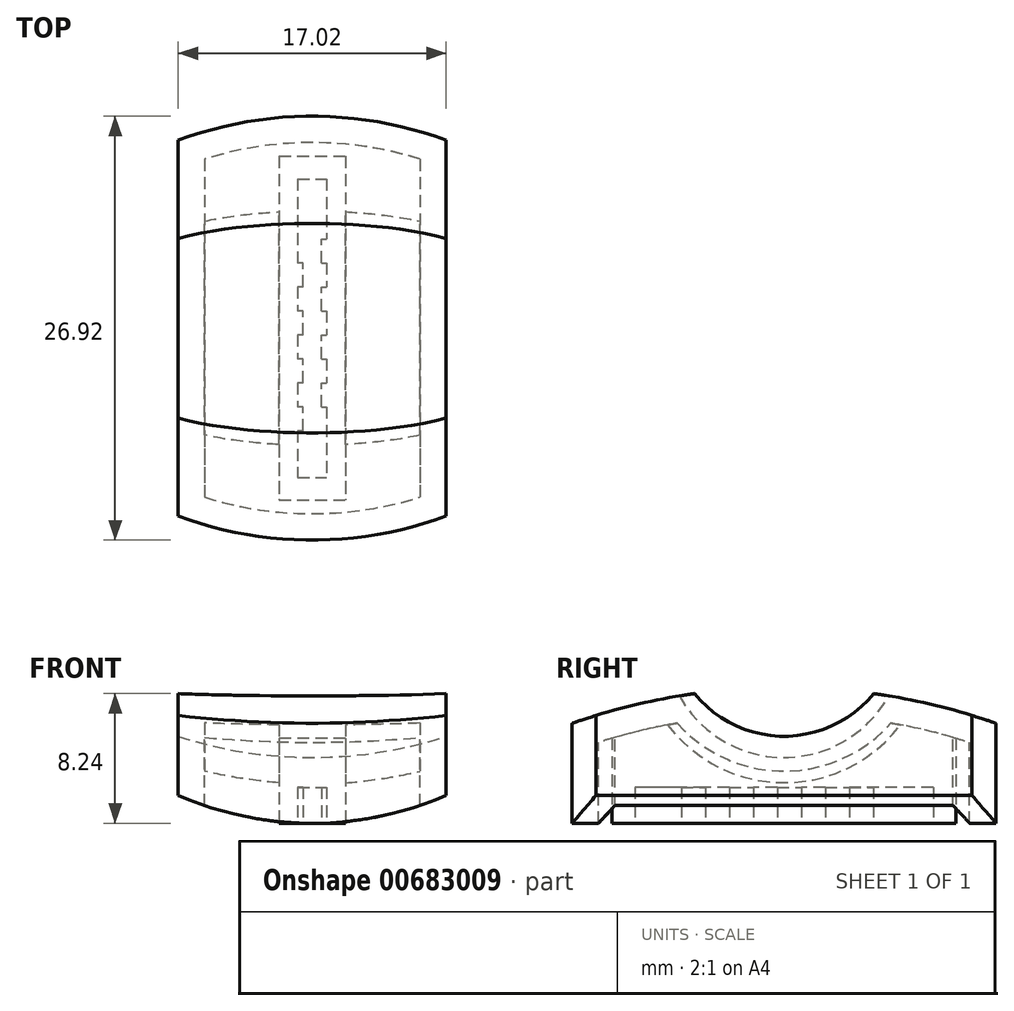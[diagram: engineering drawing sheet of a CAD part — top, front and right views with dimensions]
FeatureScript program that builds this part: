
annotation { "Feature Type Name" : "Feature", "Feature Type Description" : "" }
export const myFeature = defineFeature(function(context is Context, id is Id, definition is map)
    precondition{}
    {
        {
            var Q0;
            Q0=qCreatedBy(makeId("Top.planeOp"),FACE);
            var sketch = newSketch(context, id + "F0", { "sketchPlane" : qUnion([Q0])});
            skLineSegment(sketch, "E0.bottom", {"start": v(-8.5, 13.46) * mm, "end": v(8.5, 13.46) * mm});
            skLineSegment(sketch, "E0.top", {"start": v(-8.5, -13.46) * mm, "end": v(8.5, -13.46) * mm});
            skLineSegment(sketch, "E0.left", {"start": v(-8.5, 13.46) * mm, "end": v(-8.5, -13.46) * mm});
            skLineSegment(sketch, "E0.right", {"start": v(8.5, 13.46) * mm, "end": v(8.5, -13.46) * mm});
            skPoint(sketch, "E0.middle", {"position": v(0, 0) * mm});
            skSolve(sketch);
        }
        {
            var Q0;
            Q0 = qSketchRegion(id + "F0", true);
            extrude(context, id + "F1", {"entities" : qUnion([Q0]), "depth" : 8.64 * mm, "offsetDistance" : 25.4 * mm});
        }
        {
            var Q0;
            Q0=makeQuery(id+"F1.opExtrude","CAP_FACE",FACE,{"disambiguationData":[OSD([sQuery(id+"F0.wireOp",EDGE,"E0.bottom"),sQuery(id+"F0.wireOp",EDGE,"E0.top"),sQuery(id+"F0.wireOp",EDGE,"E0.left"),sQuery(id+"F0.wireOp",EDGE,"E0.right")])],"isStart":false});
            var sketch = newSketch(context, id + "F2", { "sketchPlane" : qUnion([Q0])});
            skArc(sketch, "E1", {"start": v(8.5, 11.94) * mm, "mid": v(0, 13.46) * mm, "end": v(-8.5, 11.94) * mm});
            skLineSegment(sketch, "E2", {"start": v(-8.5, 11.94) * mm, "end": v(8.5, 11.94) * mm, "construction": true});
            skLineSegment(sketch, "E3.bottom", {"start": v(21.07, 20.8) * mm, "end": v(-21.07, 20.8) * mm});
            skLineSegment(sketch, "E3.top", {"start": v(21.07, -42.9) * mm, "end": v(-21.07, -42.9) * mm});
            skLineSegment(sketch, "E3.left", {"start": v(21.07, 20.8) * mm, "end": v(21.07, -42.9) * mm});
            skLineSegment(sketch, "E3.right", {"start": v(-21.07, 20.8) * mm, "end": v(-21.07, -42.9) * mm});
            skLineSegment(sketch, "E4", {"start": v(8.5, 0) * mm, "end": v(-8.5, 0) * mm, "construction": true});
            skArc(sketch, "E5.MirrorCS", {"start": v(8.5, -11.94) * mm, "mid": v(0, -13.46) * mm, "end": v(-8.5, -11.94) * mm});
            skLineSegment(sketch, "E6", {"start": v(-8.5, 11.94) * mm, "end": v(-8.5, -11.94) * mm});
            skLineSegment(sketch, "E7", {"start": v(8.5, 11.94) * mm, "end": v(8.5, -11.94) * mm});
            skSolve(sketch);
        }
        {
            var Q0;
            Q0 = qSketchRegion(id + "F2", true);
            extrude(context, id + "F3", {"entities" : qUnion([Q0]), "operationType" : NewBodyOperationType.REMOVE, "endBound" : BoundingType.THROUGH_ALL, "oppositeDirection" : true, "depth" : 25.4 * mm, "offsetDistance" : 25.4 * mm});
        }
        {
            var Q0;
            Q0=qCreatedBy(makeId("Right.planeOp"),FACE);
            var sketch = newSketch(context, id + "F4", { "sketchPlane" : qUnion([Q0])});
            skLineSegment(sketch, "E8", {"start": v(-13.46, 0) * mm, "end": v(-13.46, 8.64) * mm, "construction": true});
            skLineSegment(sketch, "E9", {"start": v(13.46, 8.64) * mm, "end": v(-13.46, 8.64) * mm, "construction": true});
            skLineSegment(sketch, "E10", {"start": v(13.46, 0) * mm, "end": v(13.46, 8.64) * mm, "construction": true});
            skLineSegment(sketch, "E11", {"start": v(13.46, 0) * mm, "end": v(-13.46, 0) * mm, "construction": true});
            skArc(sketch, "E12", {"start": v(13.46, 6.35) * mm, "mid": v(0, 8.64) * mm, "end": v(-13.46, 6.35) * mm});
            skLineSegment(sketch, "E13", {"start": v(-13.46, 6.35) * mm, "end": v(13.46, 6.35) * mm, "construction": true});
            skLineSegment(sketch, "E14", {"start": v(-13.46, 6.35) * mm, "end": v(-13.46, 16.17) * mm});
            skLineSegment(sketch, "E15", {"start": v(-13.46, 16.17) * mm, "end": v(13.46, 16.17) * mm});
            skLineSegment(sketch, "E16", {"start": v(13.46, 16.17) * mm, "end": v(13.46, 6.35) * mm});
            skSolve(sketch);
        }
        {
            var Q0;
            Q0 = qSketchRegion(id + "F4", true);
            extrude(context, id + "F5", {"entities" : qUnion([Q0]), "operationType" : NewBodyOperationType.REMOVE, "endBound" : BoundingType.THROUGH_ALL, "depth" : 25.4 * mm, "offsetDistance" : 25.4 * mm, "hasSecondDirection" : true, "secondDirectionBound" : SecondDirectionBoundingType.THROUGH_ALL, "secondDirectionOppositeDirection" : true, "secondDirectionDepth" : 25.4 * mm});
        }
        {
            var Q0;
            Q0=qCreatedBy(makeId("Front.planeOp"),FACE);
            var sketch = newSketch(context, id + "F6", { "sketchPlane" : qUnion([Q0])});
            skLineSegment(sketch, "E17", {"start": v(8.5, 0) * mm, "end": v(8.5, 8.64) * mm, "construction": true});
            skLineSegment(sketch, "E18", {"start": v(-8.5, 0) * mm, "end": v(-8.5, 8.64) * mm, "construction": true});
            skLineSegment(sketch, "E19", {"start": v(8.5, 0) * mm, "end": v(-8.5, 0) * mm, "construction": true});
            skArc(sketch, "E20", {"start": v(-8.5, 1.78) * mm, "mid": v(0, 0) * mm, "end": v(8.5, 1.78) * mm});
            skLineSegment(sketch, "E21", {"start": v(8.5, 1.78) * mm, "end": v(-8.5, 1.78) * mm, "construction": true});
            skLineSegment(sketch, "E22", {"start": v(8.5, 1.78) * mm, "end": v(8.5, -5.73) * mm});
            skLineSegment(sketch, "E23", {"start": v(8.5, -5.73) * mm, "end": v(-8.5, -5.73) * mm});
            skLineSegment(sketch, "E24", {"start": v(-8.5, -5.73) * mm, "end": v(-8.5, 1.78) * mm});
            skSolve(sketch);
        }
        {
            var Q0;
            Q0 = qSketchRegion(id + "F6", true);
            extrude(context, id + "F7", {"entities" : qUnion([Q0]), "operationType" : NewBodyOperationType.REMOVE, "endBound" : BoundingType.THROUGH_ALL, "oppositeDirection" : true, "depth" : 25.4 * mm, "offsetDistance" : 25.4 * mm, "hasSecondDirection" : true, "secondDirectionBound" : SecondDirectionBoundingType.THROUGH_ALL, "secondDirectionOppositeDirection" : false, "secondDirectionDepth" : 25.4 * mm});
        }
        {
            var Q0;
            Q0=qCreatedBy(makeId("Right.planeOp"),FACE);
            var sketch = newSketch(context, id + "F8", { "sketchPlane" : qUnion([Q0])});
            skArc(sketch, "E25", {"start": v(-13.46, 6.35) * mm, "mid": v(0, 8.64) * mm, "end": v(13.46, 6.35) * mm, "construction": true});
            skArc(sketch, "E26", {"start": v(-6.65, 8.09) * mm, "mid": v(0, 4.18) * mm, "end": v(6.65, 8.09) * mm});
            skLineSegment(sketch, "E27", {"start": v(-13.46, 6.35) * mm, "end": v(13.46, 6.35) * mm, "construction": true});
            skLineSegment(sketch, "E28", {"start": v(0, 11.8) * mm, "end": v(0, 6.35) * mm, "construction": true});
            skLineSegment(sketch, "E29", {"start": v(0, 6.35) * mm, "end": v(0, 4.18) * mm, "construction": true});
            skLineSegment(sketch, "E30", {"start": v(-6.65, 8.09) * mm, "end": v(6.65, 8.09) * mm, "construction": true});
            skLineSegment(sketch, "E31", {"start": v(6.65, 8.09) * mm, "end": v(6.65, 31.75) * mm});
            skLineSegment(sketch, "E32", {"start": v(6.65, 31.75) * mm, "end": v(-6.65, 31.75) * mm});
            skLineSegment(sketch, "E33", {"start": v(-6.65, 31.75) * mm, "end": v(-6.65, 8.09) * mm});
            skSolve(sketch);
        }
        {
            var Q0;
            Q0=makeQuery(id+"F8.imprint","IMPRINT",FACE,{"disambiguationData":[TD([[makeQuery(id+"F8.imprint","IMPRINT",EDGE,{"derivedFrom":sQuery(id+"F8.wireOp",EDGE,"E26")}),1.0]])]});
            var Q1;
            Q1=sQuery(id+"F8.wireOp",EDGE,"E32");
            var Q2;
            Q2=sQuery(id+"F8.wireOp",EDGE,"E32");
            revolve(context, id + "F9", {"operationType" : NewBodyOperationType.REMOVE, "surfaceOperationType" : NewSurfaceOperationType.NEW, "entities" : qUnion([Q0]), "surfaceEntities" : qUnion([Q1]), "axis" : qUnion([Q2]), "revolveType" : RevolveType.FULL, "oppositeDirection" : true});
        }
        {
            var Q0;
            Q0=makeQuery(id+"F7.boolean.opBoolean","COPY",FACE,{"derivedFrom":makeQuery(id+"F7.opExtrude","SWEPT_FACE",FACE,{"disambiguationData":[OSD([sQuery(id+"F6.wireOp",EDGE,"E20")])]})});
            shell(context, id + "F10", {"entities" : qUnion([Q0]), "thickness" : 1.68 * mm});
        }
        {
            var Q0;
            Q0=qCreatedBy(makeId("Top.planeOp"),FACE);
            var sketch = newSketch(context, id + "F11", { "sketchPlane" : qUnion([Q0])});
            skLineSegment(sketch, "E34.bottom", {"start": v(-2.1, 10.92) * mm, "end": v(2.1, 10.92) * mm});
            skLineSegment(sketch, "E34.top", {"start": v(-2.1, -10.92) * mm, "end": v(2.1, -10.92) * mm});
            skLineSegment(sketch, "E34.left", {"start": v(-2.1, 10.92) * mm, "end": v(-2.1, -10.92) * mm});
            skLineSegment(sketch, "E34.right", {"start": v(2.1, 10.92) * mm, "end": v(2.1, -10.92) * mm});
            skPoint(sketch, "E34.middle", {"position": v(0, 0) * mm});
            skSolve(sketch);
        }
        {
            var Q0;
            Q0 = qSketchRegion(id + "F11", true);
            extrude(context, id + "F12", {"entities" : qUnion([Q0]), "operationType" : NewBodyOperationType.ADD, "endBound" : BoundingType.UP_TO_NEXT, "depth" : 25.4 * mm, "offsetDistance" : 25.4 * mm});
        }
        {
            var Q0;
            Q0=makeQuery(id+"F12.opExtrude","CAP_FACE",FACE,{"disambiguationData":[OSD([sQuery(id+"F11.wireOp",EDGE,"E34.bottom"),sQuery(id+"F11.wireOp",EDGE,"E34.top"),sQuery(id+"F11.wireOp",EDGE,"E34.left"),sQuery(id+"F11.wireOp",EDGE,"E34.right")])],"isStart":true});
            var sketch = newSketch(context, id + "F13", { "sketchPlane" : qUnion([Q0])});
            skLineSegment(sketch, "E35.bottom", {"start": v(-0.93, -9.47) * mm, "end": v(0.93, -9.47) * mm});
            skLineSegment(sketch, "E35.top", {"start": v(-0.93, 9.47) * mm, "end": v(0.93, 9.47) * mm});
            skLineSegment(sketch, "E35.left", {"start": v(-0.93, -9.47) * mm, "end": v(-0.93, 9.47) * mm});
            skLineSegment(sketch, "E35.right", {"start": v(0.93, -9.47) * mm, "end": v(0.93, 9.47) * mm});
            skPoint(sketch, "E35.middle", {"position": v(0, 0) * mm});
            skSolve(sketch);
        }
        {
            var Q0;
            Q0=makeQuery(id+"F13.imprint","IMPRINT",FACE,{"disambiguationData":[TD([[makeQuery(id+"F13.imprint","IMPRINT",EDGE,{"derivedFrom":sQuery(id+"F13.wireOp",EDGE,"E35.bottom")}),1.0]])]});
            extrude(context, id + "F14", {"entities" : qUnion([Q0]), "operationType" : NewBodyOperationType.REMOVE, "oppositeDirection" : true, "depth" : 2.3 * mm, "offsetDistance" : 25.4 * mm});
        }
        {
            var Q0;
            Q0=makeQuery(id+"F12.opExtrude","CAP_FACE",FACE,{"disambiguationData":[OSD([sQuery(id+"F11.wireOp",EDGE,"E34.bottom"),sQuery(id+"F11.wireOp",EDGE,"E34.top"),sQuery(id+"F11.wireOp",EDGE,"E34.left"),sQuery(id+"F11.wireOp",EDGE,"E34.right")])],"isStart":true});
            var sketch = newSketch(context, id + "F15", { "sketchPlane" : qUnion([Q0])});
            skLineSegment(sketch, "E36.bottom", {"start": v(0.93, -5.66) * mm, "end": v(0.6, -5.66) * mm});
            skLineSegment(sketch, "E36.top", {"start": v(0.93, -4.14) * mm, "end": v(0.6, -4.14) * mm});
            skLineSegment(sketch, "E36.left", {"start": v(0.93, -5.66) * mm, "end": v(0.93, -4.14) * mm});
            skLineSegment(sketch, "E36.right", {"start": v(0.6, -5.66) * mm, "end": v(0.6, -4.14) * mm});
            skLineSegment(sketch, "E37.bottom", {"start": v(-0.93, -4.14) * mm, "end": v(-0.6, -4.14) * mm});
            skLineSegment(sketch, "E37.top", {"start": v(-0.93, -2.62) * mm, "end": v(-0.6, -2.62) * mm});
            skLineSegment(sketch, "E37.left", {"start": v(-0.93, -4.14) * mm, "end": v(-0.93, -2.62) * mm});
            skLineSegment(sketch, "E37.right", {"start": v(-0.6, -4.14) * mm, "end": v(-0.6, -2.62) * mm});
            skLineSegment(sketch, "E38.0.1.0", {"start": v(0.6, -2.62) * mm, "end": v(0.6, -1.1) * mm});
            skLineSegment(sketch, "E38.0.1.1", {"start": v(0.93, -1.1) * mm, "end": v(0.6, -1.1) * mm});
            skLineSegment(sketch, "E38.0.1.2", {"start": v(0.93, -2.62) * mm, "end": v(0.93, -1.1) * mm});
            skLineSegment(sketch, "E38.0.1.3", {"start": v(0.93, -2.62) * mm, "end": v(0.6, -2.62) * mm});
            skLineSegment(sketch, "E38.0.2.0", {"start": v(0.6, 0.43) * mm, "end": v(0.6, 1.96) * mm});
            skLineSegment(sketch, "E38.0.2.1", {"start": v(0.93, 1.96) * mm, "end": v(0.6, 1.96) * mm});
            skLineSegment(sketch, "E38.0.2.2", {"start": v(0.93, 0.43) * mm, "end": v(0.93, 1.96) * mm});
            skLineSegment(sketch, "E38.0.2.3", {"start": v(0.93, 0.43) * mm, "end": v(0.6, 0.43) * mm});
            skLineSegment(sketch, "E38.0.3.0", {"start": v(0.6, 3.48) * mm, "end": v(0.6, 5) * mm});
            skLineSegment(sketch, "E38.0.3.1", {"start": v(0.93, 5) * mm, "end": v(0.6, 5) * mm});
            skLineSegment(sketch, "E38.0.3.2", {"start": v(0.93, 3.48) * mm, "end": v(0.93, 5) * mm});
            skLineSegment(sketch, "E38.0.3.3", {"start": v(0.93, 3.48) * mm, "end": v(0.6, 3.48) * mm});
            skLineSegment(sketch, "E38.direction1", {"start": v(0.6, -5.66) * mm, "end": v(26, -5.66) * mm, "construction": true});
            skLineSegment(sketch, "E38.direction2", {"start": v(0.6, -5.66) * mm, "end": v(0.6, -2.62) * mm, "construction": true});
            skLineSegment(sketch, "E39.0.1.0", {"start": v(-0.6, -1.1) * mm, "end": v(-0.6, 0.43) * mm});
            skLineSegment(sketch, "E39.0.1.1", {"start": v(-0.93, -1.1) * mm, "end": v(-0.6, -1.1) * mm});
            skLineSegment(sketch, "E39.0.1.2", {"start": v(-0.93, -1.1) * mm, "end": v(-0.93, 0.43) * mm});
            skLineSegment(sketch, "E39.0.1.3", {"start": v(-0.93, 0.43) * mm, "end": v(-0.6, 0.43) * mm});
            skLineSegment(sketch, "E39.0.2.0", {"start": v(-0.6, 1.96) * mm, "end": v(-0.6, 3.48) * mm});
            skLineSegment(sketch, "E39.0.2.1", {"start": v(-0.93, 1.96) * mm, "end": v(-0.6, 1.96) * mm});
            skLineSegment(sketch, "E39.0.2.2", {"start": v(-0.93, 1.96) * mm, "end": v(-0.93, 3.48) * mm});
            skLineSegment(sketch, "E39.0.2.3", {"start": v(-0.93, 3.48) * mm, "end": v(-0.6, 3.48) * mm});
            skLineSegment(sketch, "E39.0.3.0", {"start": v(-0.6, 5) * mm, "end": v(-0.6, 6.53) * mm});
            skLineSegment(sketch, "E39.0.3.1", {"start": v(-0.93, 5) * mm, "end": v(-0.6, 5) * mm});
            skLineSegment(sketch, "E39.0.3.2", {"start": v(-0.93, 5) * mm, "end": v(-0.93, 6.53) * mm});
            skLineSegment(sketch, "E39.0.3.3", {"start": v(-0.93, 6.53) * mm, "end": v(-0.6, 6.53) * mm});
            skLineSegment(sketch, "E39.direction1", {"start": v(-0.93, -4.14) * mm, "end": v(24.47, -4.14) * mm, "construction": true});
            skLineSegment(sketch, "E39.direction2", {"start": v(-0.93, -4.14) * mm, "end": v(-0.93, -1.1) * mm, "construction": true});
            skSolve(sketch);
        }
        {
            var Q0;
            Q0 = qSketchRegion(id + "F15", true);
            extrude(context, id + "F16", {"entities" : qUnion([Q0]), "operationType" : NewBodyOperationType.ADD, "endBound" : BoundingType.UP_TO_NEXT, "oppositeDirection" : true, "depth" : 25.4 * mm, "offsetDistance" : 25.4 * mm});
        }
    });
